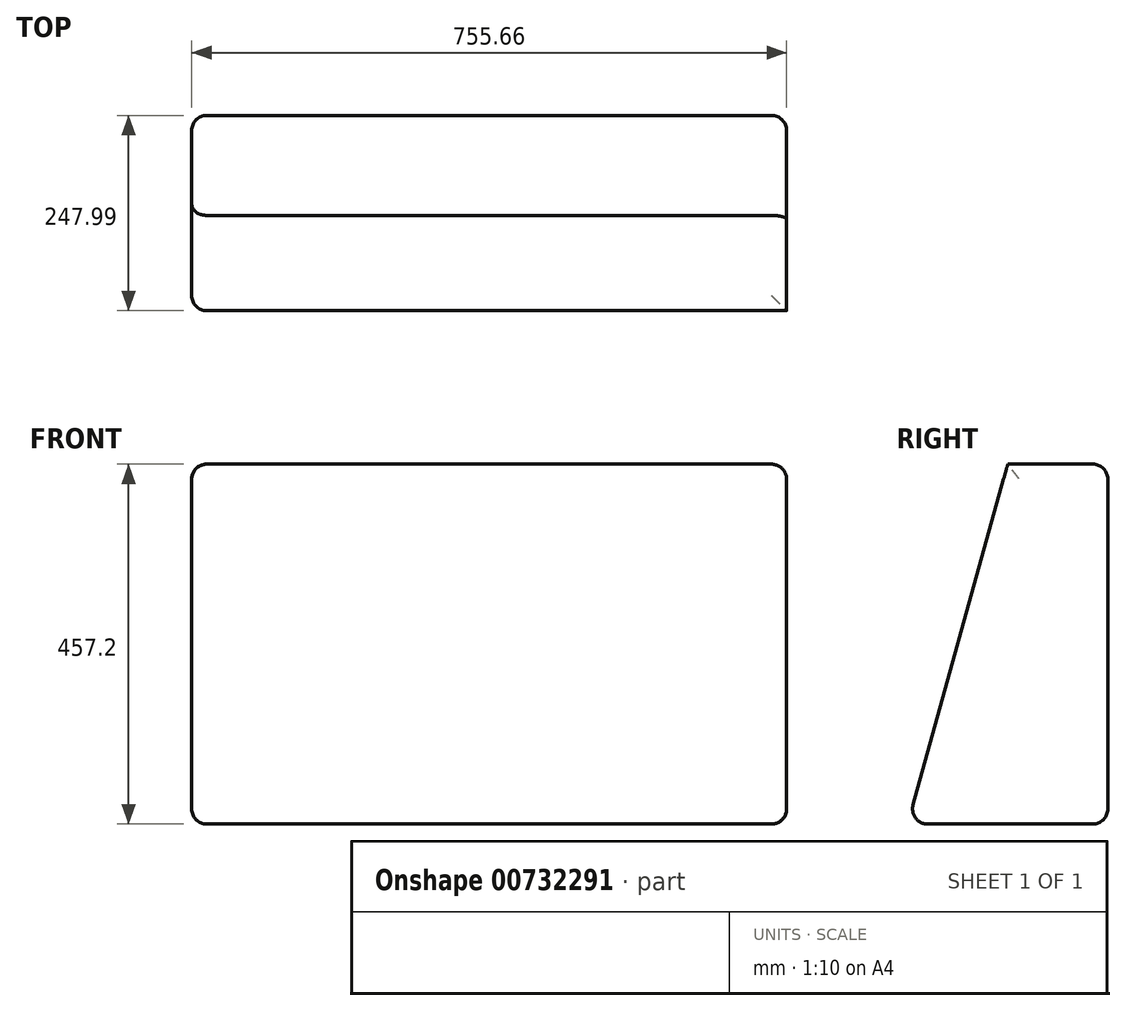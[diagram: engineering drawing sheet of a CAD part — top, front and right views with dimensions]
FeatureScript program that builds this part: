
annotation { "Feature Type Name" : "Feature", "Feature Type Description" : "" }
export const myFeature = defineFeature(function(context is Context, id is Id, definition is map)
    precondition{}
    {
        {
            var Q0;
            Q0=qCreatedBy(makeId("Top.planeOp"),FACE);
            var sketch = newSketch(context, id + "F0", { "sketchPlane" : qUnion([Q0])});
            skLineSegment(sketch, "E0.bottom", {"start": v(377.83, 127) * mm, "end": v(-377.83, 127) * mm});
            skLineSegment(sketch, "E0.top", {"start": v(377.83, -127) * mm, "end": v(-377.83, -127) * mm});
            skLineSegment(sketch, "E0.left", {"start": v(377.83, 127) * mm, "end": v(377.83, -127) * mm});
            skLineSegment(sketch, "E0.right", {"start": v(-377.83, 127) * mm, "end": v(-377.83, -127) * mm});
            skPoint(sketch, "E0.middle", {"position": v(0, 0) * mm});
            skSolve(sketch);
        }
        {
            var Q0;
            Q0=qSketchRegion(id+"F0",true);
            extrude(context, id + "F1", {"entities" : qUnion([Q0]), "depth" : 457.2 * mm, "offsetDistance" : 25.4 * mm});
        }
        {
            var Q0;
            Q0=makeQuery(id+"F1.opExtrude","SWEPT_FACE",FACE,{"disambiguationData":[OSD([sQuery(id+"F0.wireOp",EDGE,"E0.left")])]});
            var sketch = newSketch(context, id + "F2", { "sketchPlane" : qUnion([Q0])});
            skLineSegment(sketch, "E1", {"start": v(-127, 0) * mm, "end": v(0, 457.2) * mm});
            skSolve(sketch);
        }
        {
            var Q0;
            Q0=qSketchRegion(id+"F2",true);
            var Q1;
            {var subQ0=sQuery(id+"F2.wireOp",EDGE,"E1");Q1=makeQuery(id+"F2.imprint","IMPRINT",FACE,{"disambiguationData":[TD([[makeQuery(id+"F2.imprint","IMPRINT",EDGE,{"derivedFrom":subQ0}),1.0]])]});}
            extrude(context, id + "F3", {"entities" : qUnion([Q0, Q1]), "operationType" : NewBodyOperationType.REMOVE, "endBound" : BoundingType.THROUGH_ALL, "oppositeDirection" : true, "depth" : 25.4 * mm, "offsetDistance" : 25.4 * mm});
        }
        {
            var Q0;
            {var subQ0=sQuery(id+"F0.wireOp",EDGE,"E0.top");Q0=makeQuery(id+"F3.boolean.opBoolean","MERGE",EDGE,{"derivedFrom":[makeQuery(id+"F1.opExtrude","CAP_EDGE",EDGE,{"disambiguationData":[OSD([subQ0])],"isStart":true}),makeQuery(id+"F3.opExtrude","SWEPT_EDGE",EDGE,{"disambiguationData":[OSD([subQ0,sQuery(id+"F0.wireOp",EDGE,"E0.left"),sQuery(id+"F2.wireOp",EDGE,"E1")])]})]});}
            var Q1;
            Q1=makeQuery(id+"F1.opExtrude","CAP_EDGE",EDGE,{"disambiguationData":[OSD([sQuery(id+"F0.wireOp",EDGE,"E0.left")])],"isStart":true});
            var Q2;
            Q2=makeQuery(id+"F3.boolean.opBoolean","COPY",EDGE,{"derivedFrom":makeQuery(id+"F3.opExtrude","CAP_EDGE",EDGE,{"disambiguationData":[OSD([sQuery(id+"F2.wireOp",EDGE,"E1")])],"isStart":true})});
            var Q3;
            Q3=makeQuery(id+"F3.boolean.opBoolean","INTERSECT",EDGE,{"derivedFrom":[makeQuery(id+"F1.opExtrude","SWEPT_FACE",FACE,{"disambiguationData":[OSD([sQuery(id+"F0.wireOp",EDGE,"E0.right")])]}),makeQuery(id+"F3.opExtrude","SWEPT_FACE",FACE,{"disambiguationData":[OSD([sQuery(id+"F2.wireOp",EDGE,"E1")])]})]});
            var Q4;
            Q4=makeQuery(id+"F1.opExtrude","CAP_EDGE",EDGE,{"disambiguationData":[OSD([sQuery(id+"F0.wireOp",EDGE,"E0.right")])],"isStart":true});
            var Q5;
            Q5=makeQuery(id+"F1.opExtrude","CAP_EDGE",EDGE,{"disambiguationData":[OSD([sQuery(id+"F0.wireOp",EDGE,"E0.right")])],"isStart":false});
            var Q6;
            Q6=makeQuery(id+"F3.boolean.opBoolean","COPY",EDGE,{"derivedFrom":makeQuery(id+"F3.opExtrude","SWEPT_EDGE",EDGE,{"disambiguationData":[OSD([sQuery(id+"F0.wireOp",EDGE,"E0.left"),sQuery(id+"F2.wireOp",EDGE,"E1")])]})});
            var Q7;
            Q7=makeQuery(id+"F1.opExtrude","CAP_EDGE",EDGE,{"disambiguationData":[OSD([sQuery(id+"F0.wireOp",EDGE,"E0.left")])],"isStart":false});
            var Q8;
            Q8=makeQuery(id+"F1.opExtrude","SWEPT_EDGE",EDGE,{"disambiguationData":[OSD([sQuery(id+"F0.wireOp",EDGE,"E0.bottom"),sQuery(id+"F0.wireOp",EDGE,"E0.left")])]});
            var Q9;
            Q9=makeQuery(id+"F1.opExtrude","CAP_EDGE",EDGE,{"disambiguationData":[OSD([sQuery(id+"F0.wireOp",EDGE,"E0.bottom")])],"isStart":true});
            var Q10;
            Q10=makeQuery(id+"F1.opExtrude","SWEPT_EDGE",EDGE,{"disambiguationData":[OSD([sQuery(id+"F0.wireOp",EDGE,"E0.bottom"),sQuery(id+"F0.wireOp",EDGE,"E0.right")])]});
            var Q11;
            Q11=makeQuery(id+"F1.opExtrude","CAP_EDGE",EDGE,{"disambiguationData":[OSD([sQuery(id+"F0.wireOp",EDGE,"E0.bottom")])],"isStart":false});
            fillet(context, id + "F4", {"entities" : qUnion([Q0, Q1, Q2, Q3, Q4, Q5, Q6, Q7, Q8, Q9, Q10, Q11]), "radius" : 19.05 * mm, "tangentPropagation" : true, "allowEdgeOverflow" : false});
        }
    });
